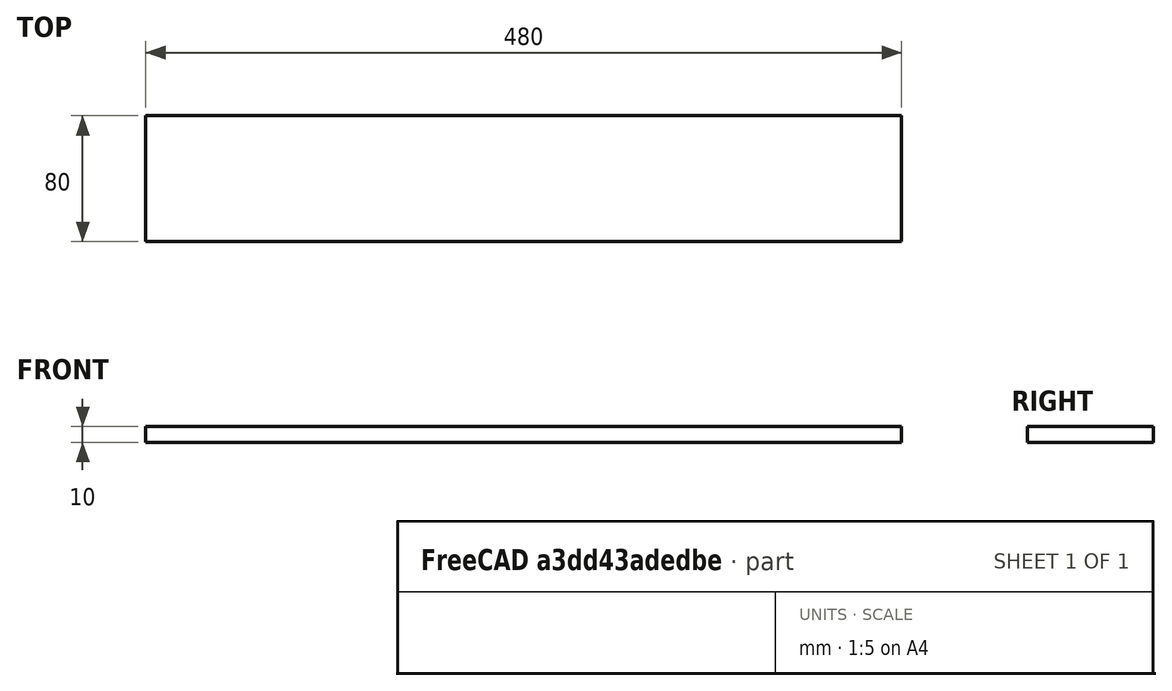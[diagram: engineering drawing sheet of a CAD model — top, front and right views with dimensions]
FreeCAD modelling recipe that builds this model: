
FCSTD DOCUMENT  (FreeCAD 0.15R4671 (Git))
Label: camion_superior
License: All rights reserved
LicenseURL: http://en.wikipedia.org/wiki/All_rights_reserved
objects: Sketcher::SketchObject×2, PartDesign::Pad×1
note: 4 computed .brp shape members not serialized (recipe doc carries the construction recipe); baked Part::Feature solids carry a one-line shape summary decoded from their .brp

FEATURE [Sketcher::SketchObject] Sketch
  sketch-geometry (4):
    g0: LineSegment StartX=-240 StartY=40 StartZ=0 EndX=240 EndY=40 EndZ=0
    g1: LineSegment StartX=240 StartY=40 StartZ=0 EndX=240 EndY=-40 EndZ=0
    g2: LineSegment StartX=240 StartY=-40 StartZ=0 EndX=-240 EndY=-40 EndZ=0
    g3: LineSegment StartX=-240 StartY=-40 StartZ=0 EndX=-240 EndY=40 EndZ=0
  constraints (12):
    c: Coincident(g0,g1)
    c: Coincident(g1,g2)
    c: Coincident(g2,g3)
    c: Coincident(g3,g0)
    c: Horizontal(g0)
    c: Horizontal(g2)
    c: Vertical(g1)
    c: Vertical(g3)
    c: DistanceX(g0) = 480
    c: DistanceY(g1) = -80
    c: DistanceX(g-1,g1) = 240
    c: DistanceY(g-1,g0) = 40
FEATURE [Sketcher::SketchObject] Sketch001
  sketch-geometry (4):
    g0: LineSegment StartX=-240 StartY=40 StartZ=0 EndX=240 EndY=40 EndZ=0
    g1: LineSegment StartX=240 StartY=40 StartZ=0 EndX=240 EndY=-40 EndZ=0
    g2: LineSegment StartX=240 StartY=-40 StartZ=0 EndX=-240 EndY=-40 EndZ=0
    g3: LineSegment StartX=-240 StartY=-40 StartZ=0 EndX=-240 EndY=40 EndZ=0
  constraints (12):
    c: Coincident(g0,g1)
    c: Coincident(g1,g2)
    c: Coincident(g2,g3)
    c: Coincident(g3,g0)
    c: Horizontal(g0)
    c: Horizontal(g2)
    c: Vertical(g1)
    c: Vertical(g3)
    c: DistanceX(g0) = 480
    c: DistanceY(g3) = 80
    c: DistanceX(g-1,g0) = -240
    c: DistanceY(g-1,g2) = -40
FEATURE [PartDesign::Pad] Pad
  Length = 10
  Length2 = 100
  Sketch = -> Sketch001
  Type = 0
